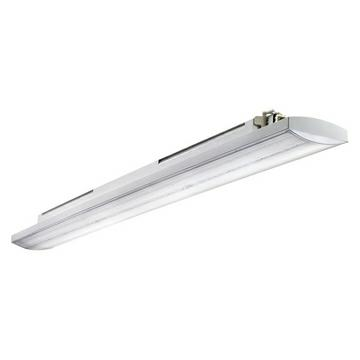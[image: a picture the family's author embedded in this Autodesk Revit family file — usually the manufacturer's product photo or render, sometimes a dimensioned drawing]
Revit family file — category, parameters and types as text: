
# Revit family: Lighting-Industriale-GEWISS-SMART[3]-PLAFONIERA-LED_TRASPARENTE_800mm
name_source: partatom
category: Apparecchi per illuminazione
units: mm (PartAtom-declared; Revit-internal decimal feet)

## family parameters
Condiviso = No
Host = Superficie
Punto di calcolo locali = Sì
Quota connettore circolare = Usa diametro
Sorgente d'illuminazione = No
Taglio con vuoti quando caricato = No
Tipo di parte = Normale

## types (1)
- Lighting-Industriale-GEWISS-SMART[3]-PLAFONIERA-LED_TRASPARENTE_800mm
    Alimentatore = Incluso
    Apparecchio a ridotta temperatura superficiale = Si
    Applicazione = Interno
    Cablaggio = Con connettore stagno Gw connect
    Cablaggio : = Passante
    Caratteristiche elettriche e gestione della luce = -
    Caratteristiche ottiche e illuminotecniche = -
    Catalogo = LIGHTING
    Catalogo Serie = SMART [3]
    Certificazione DIN 18032-3 = Non disponibile
    Certificazioni e classificazioni = -
    Classe di efficienza LED integrati = A ÷ A++
    Classe fotobiologica = RG0
    Classe isolamento = II
    Classificazione: = -
    Codice Electrocod = 2434
    Codice digitale univoco (Datamatrix) = Datamatrix
    Colore = Grigio (RAL 7035)
    Contesto = Illuminazione di magazzini, parcheggi coperti e locali produttivi industriali
    Controllo abbagliamento e luminanza = UGR - 25 (4H/8H)
    Corpo = Policarbonato
    Descrizione = SMART3 LED 800 1X18 TRASPAR.LP
    Dispositivo di protezione = DM 1KV / CM 2KV
    Durata di vita = L90B50 (Tq+25°C) = 50.000h - L80B10 (Tq+25°C) = 100.000h
    Efficienza luminosa (lm/W) = 100
    Failure rate apparecchio (35.000h, Tq=35° C) = <2,5%
    Failure rate apparecchio (50.000h, Tq=25° C) = <2,5%
    Finitura colore = PC colorato in pasta RAL7035
    Fissaggio = Supporto in acciaio INOX
    Flusso nominale (lm) = 2100
    Frequenza nominale (Hz) = 50/60 Hz
    Ganci = GEWISS  - ALLUMINIO
    Gancio di chiusura = -
    Garanzia = 5 anni
    Glow Wire Test = 850°C
    Grado di protezione = IP66/IP69
    Gruppo ottico = Integrato nello schermo
    Guarnizioni = Sigillante depositato a CNC
    IDF = 839ae22e-8b0c-4fd9-88d1-b9beb72ccc37
    IDT = 7ab7d349bce84d43a9e106559738b684
    IPEA = -
    Immagine tipo = GWS3118T.jpg
    Inclinazione = Con staffa di fissaggio
    Indice di resa cromatica = CRI-80
    Informazioni generali = -
    Installazione e manutenzione = -
    LED Life time (L80B50) = 100000H
    LED Life time (L90B50) = 50000H
    LED LifeTime (L80B20) = 85000H
    Lampada = LED
    Lampada: = LED
    Lumen output (lm) = 1500
    Lunghezza = 800 mm
    Lunghezza Lampada = 800 mm  [stored 2.62467 ft]
    Materiali = -
    Modello = GWS3118TL
    Norma di riferimento = EN60598-1; IEC 62778; IEC62471
    Ottica = Trasparente microprismato
    Peso (kg): = 1,5
    Potenza di sistema = 15W
    Produttore = GEWISS S.p.A.
    Prospetto di default = 1219 mm
    Resistenza agli urti = IK08
    Resistenza al filo incandescente = 850 °C
    Resistenza alle sovratensioni : = 2KV in modalità comune; 1KV in modalità differenziale
    SEO = Plafoniera
    Scheda Tecnica = https://www.gewiss.com
    Schermo = Policarbonato stabilizzato agli UV
    Schermo- = Gewiss - Led Acceso
    Sistema di controllo = Linea Passante - On / Off
    Sistema di controllo : = ON / OFF
    Sostituibilità gruppo ottico = Non disponibile
    Sostituibilità piastra di cablaggio = Non disponibile
    Stampa 1_100 = Sì
    Stampa 1_200 = No
    Struttura = GEWISS - SMART 3 - GRIGIO
    Superficie massima esposta al vento : = -
    Temperatura di colore = 4000K
    Temperatura di colore: = 4000 K (CRI>80)
    Temperatura di esercizio = -25 +50 °C
    Temperatura di stoccaggio = -25 +80 °C
    Temperatura di utilizzo = -30 +50 °C
    Tensione = 220/240 V - 50/60 Hz - Stand alone
    Tensione di alimentazione = 220 - 240 V
    Tipo alimentatore = Driver Led in corrente continua
    Tipo di apparecchio = Apparecchio a LED per illuminazione generale
    Tipo di installazione e montaggio = Plafone - Parete - Sospensione
    Tipologia = Stand alone - Cablaggio passante
    Tipologia sorgente luminosa = LED - Non sostituibile
    Tolleranza cromatica = SDCM = 3
    URL = https://www.gewiss.com
    Vano di alimentazione = Integrato
    Versione file RFA = 20.11
    Viti esterne = -

note: [stored X ft] marks values corroborated as IEEE doubles in the binary element streams (Revit-internal decimal feet)
